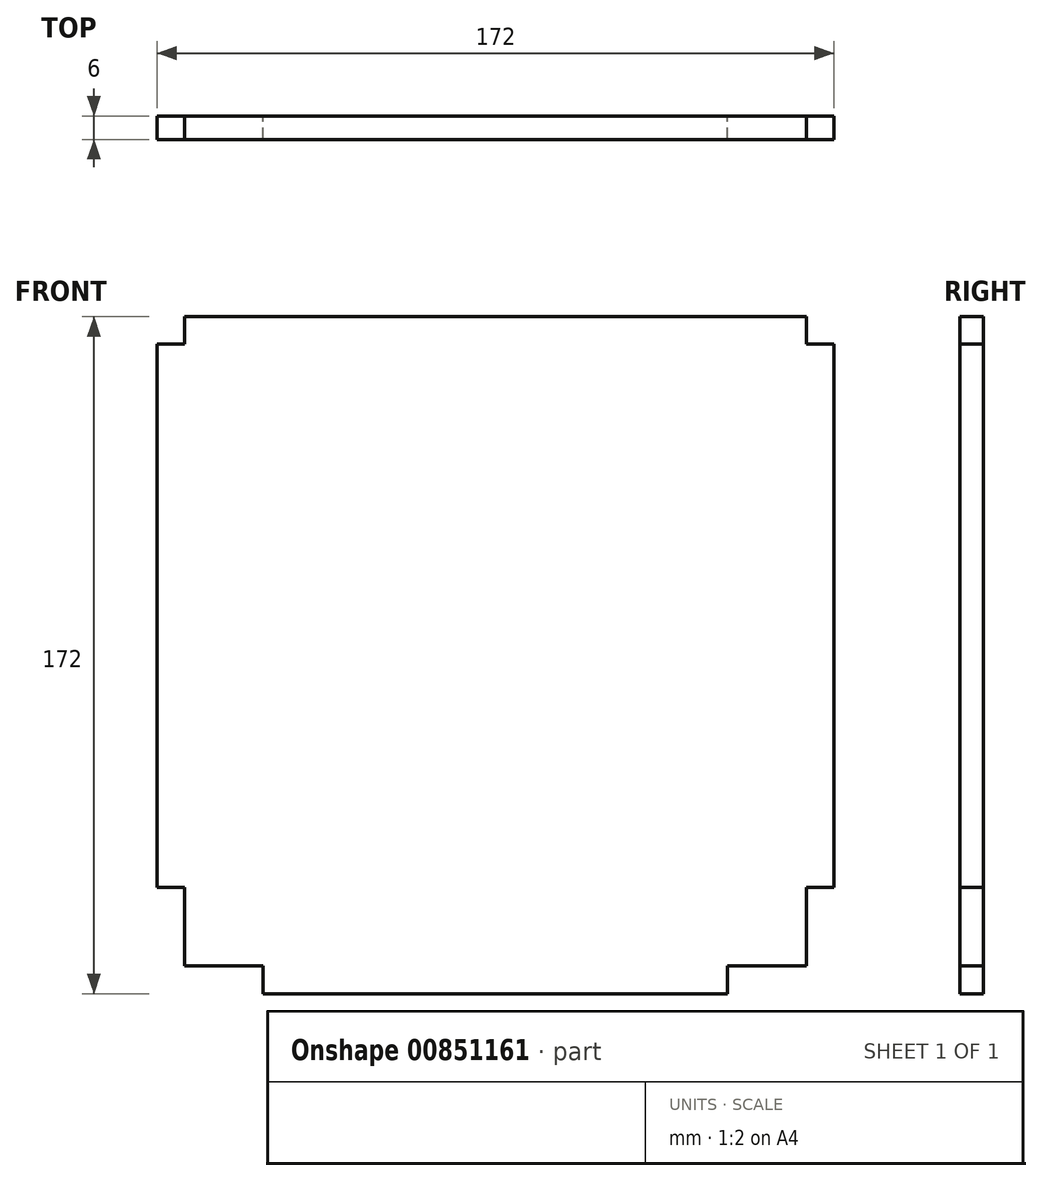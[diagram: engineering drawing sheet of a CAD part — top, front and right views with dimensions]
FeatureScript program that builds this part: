
annotation { "Feature Type Name" : "Feature", "Feature Type Description" : "" }
export const myFeature = defineFeature(function(context is Context, id is Id, definition is map)
    precondition{}
    {
        {
            var Q0;
            Q0=qCreatedBy(makeId("Front.planeOp"),FACE);
            var sketch = newSketch(context, id + "F0", { "sketchPlane" : qUnion([Q0])});
            skLineSegment(sketch, "E0.bottom", {"start": v(79, 86) * mm, "end": v(-79, 86) * mm});
            skLineSegment(sketch, "E0.top", {"start": v(59, -86) * mm, "end": v(-59, -86) * mm});
            skLineSegment(sketch, "E0.left", {"start": v(86, 79) * mm, "end": v(86, -59) * mm});
            skLineSegment(sketch, "E0.right", {"start": v(-86, 79) * mm, "end": v(-86, -59) * mm});
            skPoint(sketch, "E0.middle", {"position": v(0, 0) * mm});
            skLineSegment(sketch, "E1.top", {"start": v(-86, 79) * mm, "end": v(-79, 79) * mm});
            skLineSegment(sketch, "E1.right", {"start": v(-79, 86) * mm, "end": v(-79, 79) * mm});
            skLineSegment(sketch, "E2.MirrorCS", {"start": v(79, 86) * mm, "end": v(79, 79) * mm});
            skLineSegment(sketch, "E3.MirrorCS", {"start": v(86, 79) * mm, "end": v(79, 79) * mm});
            skLineSegment(sketch, "E4", {"start": v(-86, -59) * mm, "end": v(-79, -59) * mm});
            skLineSegment(sketch, "E5", {"start": v(-79, -59) * mm, "end": v(-79, -79) * mm});
            skLineSegment(sketch, "E6", {"start": v(-79, -79) * mm, "end": v(-59, -79) * mm});
            skLineSegment(sketch, "E7", {"start": v(-59, -79) * mm, "end": v(-59, -86) * mm});
            skLineSegment(sketch, "E8.MirrorCS", {"start": v(86, -59) * mm, "end": v(79, -59) * mm});
            skLineSegment(sketch, "E9.MirrorCS", {"start": v(79, -59) * mm, "end": v(79, -79) * mm});
            skLineSegment(sketch, "E10.MirrorCS", {"start": v(79, -79) * mm, "end": v(59, -79) * mm});
            skLineSegment(sketch, "E11.MirrorCS", {"start": v(59, -79) * mm, "end": v(59, -86) * mm});
            skPoint(sketch, "E12.orphan", {"position": v(-86, -86) * mm});
            skPoint(sketch, "E13.orphan", {"position": v(86, -86) * mm});
            skPoint(sketch, "E14.orphan", {"position": v(-86, 86) * mm});
            skPoint(sketch, "E15.orphan", {"position": v(86, 86) * mm});
            skSolve(sketch);
        }
        {
            var Q0;
            Q0 = qSketchRegion(id + "F0", true);
            extrude(context, id + "F1", {"entities" : qUnion([Q0]), "depth" : 6 * mm, "offsetDistance" : 25 * mm});
        }
    });
